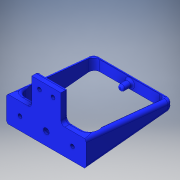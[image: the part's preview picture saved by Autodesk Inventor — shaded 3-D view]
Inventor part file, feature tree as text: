
AUTODESK INVENTOR PART (.ipt)
format: ipt  version: 2016 (Build 200138000, 138)  size: 366,080 bytes
history: native  units: in
note: dims shown in document units (in); Inventor stores cm internally (conversion verified against a paired STEP export)
features: sketch x11, other x3
ambient origin geometry x8: Origin, YZ Plane, XZ Plane, XY Plane, X Axis, Y Axis, Z Axis, Center Point
bodies: Solid1 (feature_tree)
feature tree (14):
  other  "Knee_hip_joint_right_side.ipt"
  other  "Solid1::Knee_hip_joint_right_side.ipt"
  other  "TaggingFeature1"
  sketch  "Sketch1"  dims[d0=0.3937in]
  sketch  "Sketch16"
  sketch  "Sketch17"
  sketch  "Sketch19"
  sketch  "Sketch20"
  sketch  "Sketch22"
  sketch  "Sketch24"
  sketch  "Sketch25"
  sketch  "Sketch30"
  sketch  "Sketch31"
  sketch  "Sketch32"
